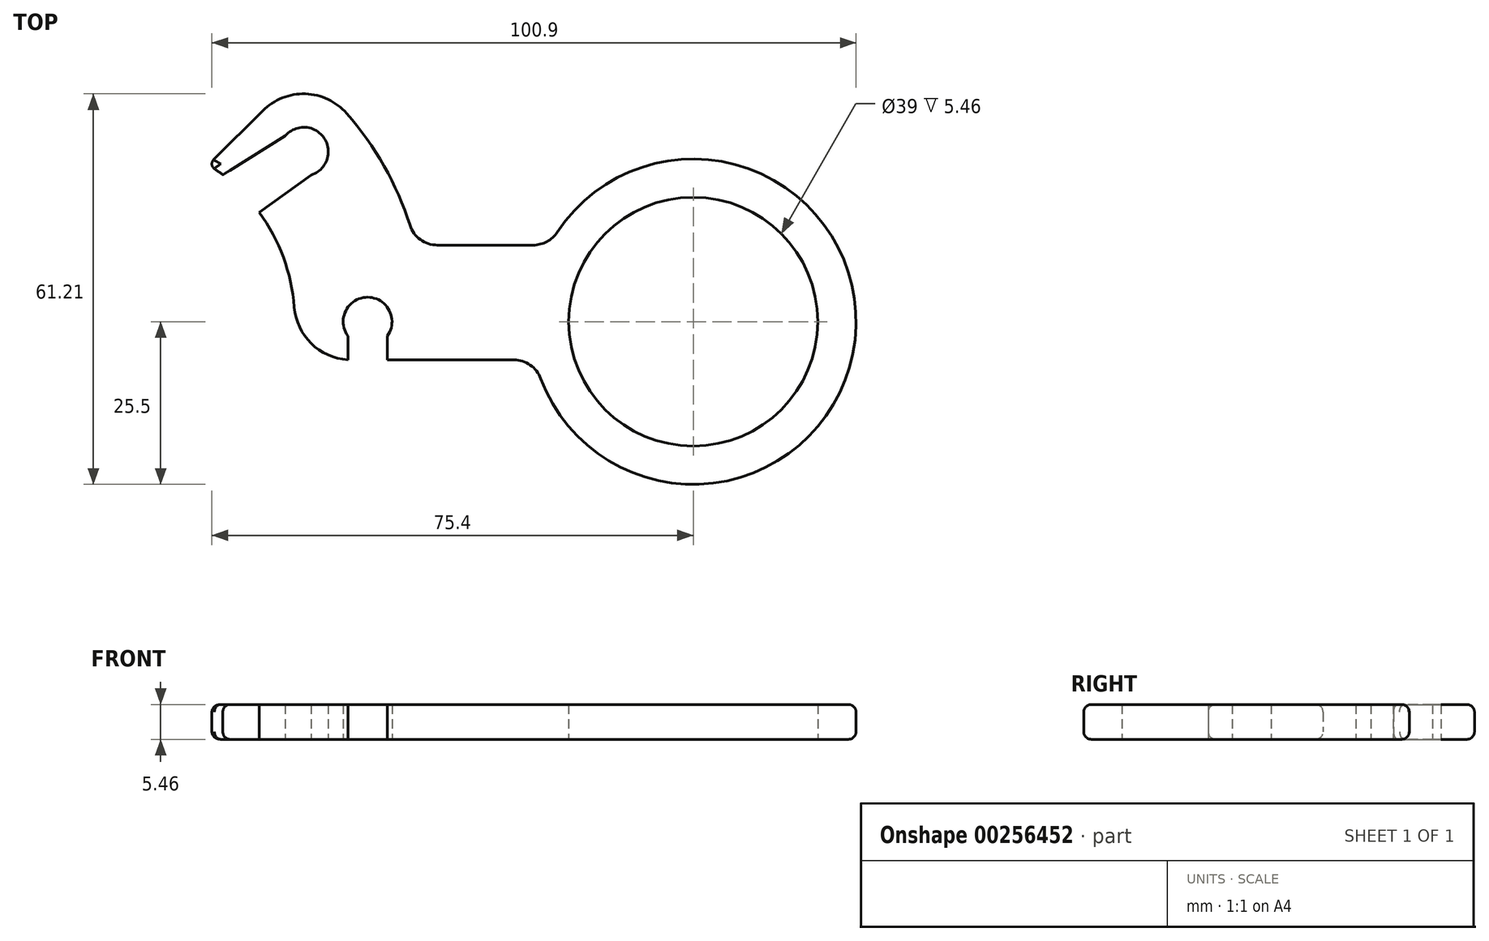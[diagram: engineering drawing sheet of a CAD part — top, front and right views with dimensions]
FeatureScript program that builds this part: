
annotation { "Feature Type Name" : "Feature", "Feature Type Description" : "" }
export const myFeature = defineFeature(function(context is Context, id is Id, definition is map)
    precondition{}
    {
        {
            var Q0;
            Q0=qCreatedBy(makeId("Top.planeOp"),FACE);
            var sketch = newSketch(context, id + "F0", { "sketchPlane" : qUnion([Q0])});
            skCircle(sketch, "E0", {"center": v(0, 0) * mm, "radius": 13.5 * mm, "construction": true});
            skCircle(sketch, "E1", {"center": v(13.5, 0) * mm, "radius": 9.2 * mm, "construction": true});
            skLineSegment(sketch, "E2", {"start": v(10.17, 8.88) * mm, "end": v(-3, 0) * mm, "construction": true});
            skArc(sketch, "E3", {"start": v(9.67, 0.76) * mm, "mid": v(9.1, 3.36) * mm, "end": v(7.85, 5.7) * mm});
            skArc(sketch, "E4", {"start": v(15.71, 5.04) * mm, "mid": v(14.36, 8.13) * mm, "end": v(12.4, 10.88) * mm});
            skCircle(sketch, "E5", {"center": v(30.5, 0) * mm, "radius": 6.5 * mm});
            skArc(sketch, "E6", {"start": v(22.54, -2.98) * mm, "mid": v(38.95, -0.95) * mm, "end": v(23.4, 4.68) * mm});
            skLineSegment(sketch, "E7", {"start": v(12.47, -2) * mm, "end": v(12.66, -2) * mm});
            skLineSegment(sketch, "E8", {"start": v(5.46, 8.45) * mm, "end": v(8.03, 11.02) * mm});
            skArc(sketch, "E9", {"start": v(10.54, 7.66) * mm, "mid": v(11.24, 9.58) * mm, "end": v(9.2, 9.71) * mm});
            skArc(sketch, "E10", {"start": v(14.53, -0.75) * mm, "mid": v(13.5, 1.28) * mm, "end": v(12.47, -0.75) * mm});
            skLineSegment(sketch, "E11", {"start": v(12.47, -0.75) * mm, "end": v(12.47, -2) * mm});
            skLineSegment(sketch, "E12", {"start": v(14.53, -0.75) * mm, "end": v(14.53, -2) * mm});
            skLineSegment(sketch, "E13.trimOffspring", {"start": v(14.53, -2) * mm, "end": v(21.13, -2) * mm});
            skLineSegment(sketch, "E14", {"start": v(17.14, 4) * mm, "end": v(22.15, 4) * mm});
            skLineSegment(sketch, "E15", {"start": v(7.85, 5.7) * mm, "end": v(10.54, 7.66) * mm});
            skLineSegment(sketch, "E16", {"start": v(9.2, 9.71) * mm, "end": v(6.05, 7.58) * mm, "construction": true});
            skLineSegment(sketch, "E17", {"start": v(9.2, 9.71) * mm, "end": v(5.94, 7.67) * mm});
            skArc(sketch, "E18.trimOffspring", {"start": v(5.94, 7.67) * mm, "mid": v(5.72, 7.83) * mm, "end": v(5.5, 8) * mm});
            skPoint(sketch, "E19.visualSharp", {"position": v(10.07, 13.07) * mm});
            skArc(sketch, "E19.filletArc", {"start": v(12.4, 10.88) * mm, "mid": v(10.25, 11.9) * mm, "end": v(8.03, 11.02) * mm});
            skPoint(sketch, "E20.visualSharp", {"position": v(9.5, -2) * mm});
            skArc(sketch, "E20.filletArc", {"start": v(9.67, 0.76) * mm, "mid": v(10.62, -1.2) * mm, "end": v(12.66, -2) * mm});
            skPoint(sketch, "E21.visualSharp", {"position": v(23, 4) * mm});
            skArc(sketch, "E21.filletArc", {"start": v(22.15, 4) * mm, "mid": v(22.86, 4.18) * mm, "end": v(23.4, 4.67) * mm});
            skPoint(sketch, "E22.visualSharp", {"position": v(22.24, -2) * mm});
            skArc(sketch, "E22.filletArc", {"start": v(22.54, -2.97) * mm, "mid": v(21.99, -2.27) * mm, "end": v(21.13, -2) * mm});
            skPoint(sketch, "E23.visualSharp", {"position": v(16, 4) * mm});
            skArc(sketch, "E23.filletArc", {"start": v(15.71, 5.04) * mm, "mid": v(16.26, 4.29) * mm, "end": v(17.14, 4) * mm});
            skPoint(sketch, "E24.visualSharp", {"position": v(5.2, 8.2) * mm});
            skArc(sketch, "E24.filletArc", {"start": v(5.46, 8.45) * mm, "mid": v(5.37, 8.21) * mm, "end": v(5.5, 8) * mm});
            skLineSegment(sketch, "E25", {"start": v(13.5, 0) * mm, "end": v(13.5, -2) * mm, "construction": true});
            skSolve(sketch);
        }
        {
            var Q0;
            {var subQ3=sQuery(id+"F0.wireOp",EDGE,"E7");var subQ6=sQuery(id+"F0.wireOp",EDGE,"E3");Q0=qUnion([makeQuery(id+"F0.imprint","IMPRINT",FACE,{"disambiguationData":[TD([[makeQuery(id+"F0.imprint","IMPRINT",EDGE,{"derivedFrom":subQ3}),1.0]])]}),makeQuery(id+"F0.imprint","IMPRINT",FACE,{"disambiguationData":[TD([[makeQuery(id+"F0.imprint","IMPRINT",EDGE,{"derivedFrom":subQ6}),-1.0]])]})]);}
            extrude(context, id + "F1", {"entities" : qUnion([Q0]), "flatOperationType" : FlatOperationType.REMOVE, "depth" : 1.82 * mm, "offsetDistance" : 25 * mm, "domain" : OperationDomain.MODEL});
        }
        {
            var Q0;
            Q0=makeQuery(id+"F1.opExtrude","CAP_EDGE",EDGE,{"disambiguationData":[OSD([sQuery(id+"F0.wireOp",EDGE,"E13.trimOffspring")])],"isStart":false});
            var Q1;
            Q1=makeQuery(id+"F1.opExtrude","CAP_EDGE",EDGE,{"disambiguationData":[OSD([sQuery(id+"F0.wireOp",EDGE,"E13.trimOffspring")])],"isStart":true});
            fillet(context, id + "F2", {"entities" : qUnion([Q0, Q1]), "radius" : 0.4 * mm, "tangentPropagation" : true, "allowEdgeOverflow" : false});
        }
        {
            var Q0;
            Q0=makeQuery(id+"F1.opExtrude","SWEPT_BODY",BODY,{"disambiguationData":[OSD([sQuery(id+"F0.wireOp",EDGE,"E7"),sQuery(id+"F0.wireOp",EDGE,"E11"),sQuery(id+"F0.wireOp",EDGE,"E20.filletArc")])]});
            deleteBodies(context, id + "F3", {"entities" : qUnion([Q0])});
        }
        {
            var Q0;
            Q0=makeQuery(id+"F1.opExtrude","SWEPT_BODY",BODY,{"disambiguationData":[OSD([sQuery(id+"F0.wireOp",EDGE,"E3"),sQuery(id+"F0.wireOp",EDGE,"E4"),sQuery(id+"F0.wireOp",EDGE,"E5"),sQuery(id+"F0.wireOp",EDGE,"E6"),sQuery(id+"F0.wireOp",EDGE,"E8"),sQuery(id+"F0.wireOp",EDGE,"E9"),sQuery(id+"F0.wireOp",EDGE,"E10"),sQuery(id+"F0.wireOp",EDGE,"E11"),sQuery(id+"F0.wireOp",EDGE,"E12"),sQuery(id+"F0.wireOp",EDGE,"E13.trimOffspring"),sQuery(id+"F0.wireOp",EDGE,"E14"),sQuery(id+"F0.wireOp",EDGE,"E15"),sQuery(id+"F0.wireOp",EDGE,"E17"),sQuery(id+"F0.wireOp",EDGE,"E18.trimOffspring"),sQuery(id+"F0.wireOp",EDGE,"E19.filletArc"),sQuery(id+"F0.wireOp",EDGE,"E20.filletArc"),sQuery(id+"F0.wireOp",EDGE,"E21.filletArc"),sQuery(id+"F0.wireOp",EDGE,"E22.filletArc"),sQuery(id+"F0.wireOp",EDGE,"E23.filletArc"),sQuery(id+"F0.wireOp",EDGE,"E24.filletArc")])]});
            var Q1;
            Q1=qCreatedBy(makeId("Origin.pointOp"),VERTEX);
            transform(context, id + "F4", {"entities" : qUnion([Q0]), "transformType" : TransformType.SCALE_UNIFORMLY, "scale" : 3, "makeCopy" : false, "scalePoint" : qUnion([Q1])});
        }
    });
